# Revit family: Lin1-9.84ft-Double Head
name_source: partatom
category: Lighting Fixtures
units: mm (PartAtom-declared; Revit-internal decimal feet)

## family parameters
Always vertical = Yes
Cut with Voids When Loaded = No
Light Source = No
Maintain Annotation Orientation = No
OmniClass Number = 23.80.70.00
OmniClass Title = Lighting
Part Type = Normal
Room Calculation Point = No
Round Connector Dimension = Use Diameter
Shared = No
Work Plane-Based = No

## types (16) — shared parameters
CRI = 80
Default Elevation = 0' - 0"
H = 9' - 10 3/32"
IP Rating = IP65
Input Voltage = 120-277V
Lamp = LED
Load Classification = Lighting
Manufacturer = Above All Lighting
Power Factor = 0.9
URL = https://www.abovealllighting.com

## per-type parameters (varying)
| type | IES | Model | Wattage Comments |
| LIN1-30W-3000K-II-9.84ft | IES : 30W-II | LIN1-3030801-II-BK | 30W |
| LIN1-30W-3000K-III-9.84ft | IES : 30W-III | LIN1-3030801-III-BK | 30W |
| LIN1-30W-3000K-IV-9.84ft | IES : 30W-IV | LIN1-3030801-IV-BK | 30W |
| LIN1-30W-3000K-V-9.84ft | IES : 30W-V | LIN1-3030801-V-BK | 30W |
| LIN1-40W-3000K-II-9.84ft | IES : 40W-II | LIN1-4030801-II-BK | 40W |
| LIN1-40W-3000K-III-9.84ft | IES : 40W-III | LIN1-4030801-III-BK | 40W |
| LIN1-40W-3000K-IV-9.84ft | IES : 40W-IV | LIN1-4030801-IV-BK | 40W |
| LIN1-40W-3000K-V-9.84ft | IES : 40W-V | LIN1-4030801-V-BK | 40W |
| LIN1-50W-3000K-II-9.84ft | IES : 50W-II | LIN1-5030801-II-BK | 50W |
| LIN1-50W-3000K-III-9.84ft | IES : 50W-III | LIN1-5030801-III-BK | 50W |
| LIN1-50W-3000K-IV-9.84ft | IES : 50W-IV | LIN1-5030801-IV-BK | 50W |
| LIN1-50W-3000K-V-9.84ft | IES : 50W-V | LIN1-5030801-V-BK | 50W |
| LIN1-60W-3000K-II-9.84ft | IES : 60W-II | LIN1-6030801-II-BK | 60W |
| LIN1-60W-3000K-III-9.84ft | IES : 60W-III | LIN1-6030801-III-BK | 60W |
| LIN1-60W-3000K-IV-9.84ft | IES : 60W-IV | LIN1-6030801-IV-BK | 60W |
| LIN1-60W-3000K-V-9.84ft | IES : 60W-V | LIN1-6030801-V-BK | 60W |

## geometry (parser evidence)
native form markers: Sweep x6
no freeform markers — native parametric forms only
